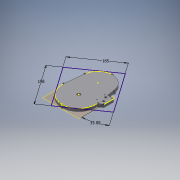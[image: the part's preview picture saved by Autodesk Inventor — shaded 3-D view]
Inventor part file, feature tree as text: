
AUTODESK INVENTOR PART (.ipt)
format: ipt  version: 2017 (Build 210142000, 142)  size: 462,336 bytes
history: native  units: mm
features: extrude x9, sketch x9, other x7, projected_geometry x6, reference x5, plane x2
ambient origin geometry x8: Origin, YZ Plane, XZ Plane, XY Plane, X Axis, Y Axis, Z Axis, Center Point
bodies: Solid1 (feature_tree)
feature tree (38):
  plane  "Work Plane1"
  extrude  "Extrusion1"  Depth=55.0mm
  extrude  "Extrusion2"  Depth=10.0mm TaperAngle=0.0deg
  extrude  "Extrusion3"  Depth=2.0mm TaperAngle=0.0deg
  extrude  "Extrusion5"  Depth=80.0mm
  extrude  "Extrusion6"  Depth=8.0mm
  sketch  "Sketch7"  dims[d12=40.0mm d13=12.0mm]
  extrude  "Extrusion7"  Depth=12.0mm
  extrude  "Extrusion8"  Depth=10.0mm
  extrude  "Extrusion9"  Depth=45.0mm
  sketch  "Sketch9"  dims[d19=2.5mm d20=45.0mm]
  plane  "Work Plane2"
  extrude  "Extrusion10"  Depth=10.0mm TaperAngle=0.0deg
  sketch  "Sketch10"  dims[d21=20.0mm d22=10.0mm d23=0.0mm d24=10.0mm d25=0.0mm d26=3.81mm d27=8.0mm d28=10.0mm d29=0.0mm d30=10.0mm d31=0.0mm d32=2.794mm d33=4.0mm d34=33.0mm d35=28.0mm d36=10.0mm d37=0.0mm d38=30.0deg d39=10.0mm d40=0.0mm d41=198.0mm d42=185.0mm d43=6.108652mm d44=13.5mm]
  sketch  "Sketch1"  dims[d0=65.0mm d1=55.0mm]
  reference  "Reference1"
  reference  "Reference2"
  reference  "Reference3"
  reference  "Reference4"
  sketch  "Sketch2"  dims[d2=5.0mm d3=10.0mm d4=0.0mm]
  projected_geometry  "Projected Loop1"
  sketch  "Sketch3"  dims[d5=13.5mm d6=2.0mm d7=0.0mm]
  projected_geometry  "Projected Loop2"
  sketch  "Sketch5"  dims[d8=80.0mm d9=20.0mm]
  reference  "Reference5"
  sketch  "Sketch6"  dims[d10=3.490659mm d11=8.0mm]
  projected_geometry  "Projected Loop3"
  projected_geometry  "Projected Loop4"
  sketch  "Sketch8"  dims[d14=10.0mm d15=0.0mm d18=65.0mm]
  projected_geometry  "Projected Loop5"
  projected_geometry  "Projected Loop6"
  parser-record x1  (decoder bookkeeping rows leaked as tree rows — omitted from the tree; the rows remain in map.json)
  other  "gearbox.iam"
  other  "6003 bearing:4"
  other  "6003 bearing:8"
  other  "Spur Gears:1"
  other  "Spur Gear2:1"
  other  "Spur Gears:3"
note: 1 file-system path scrubbed to <path> (originals preserved in map.json)
